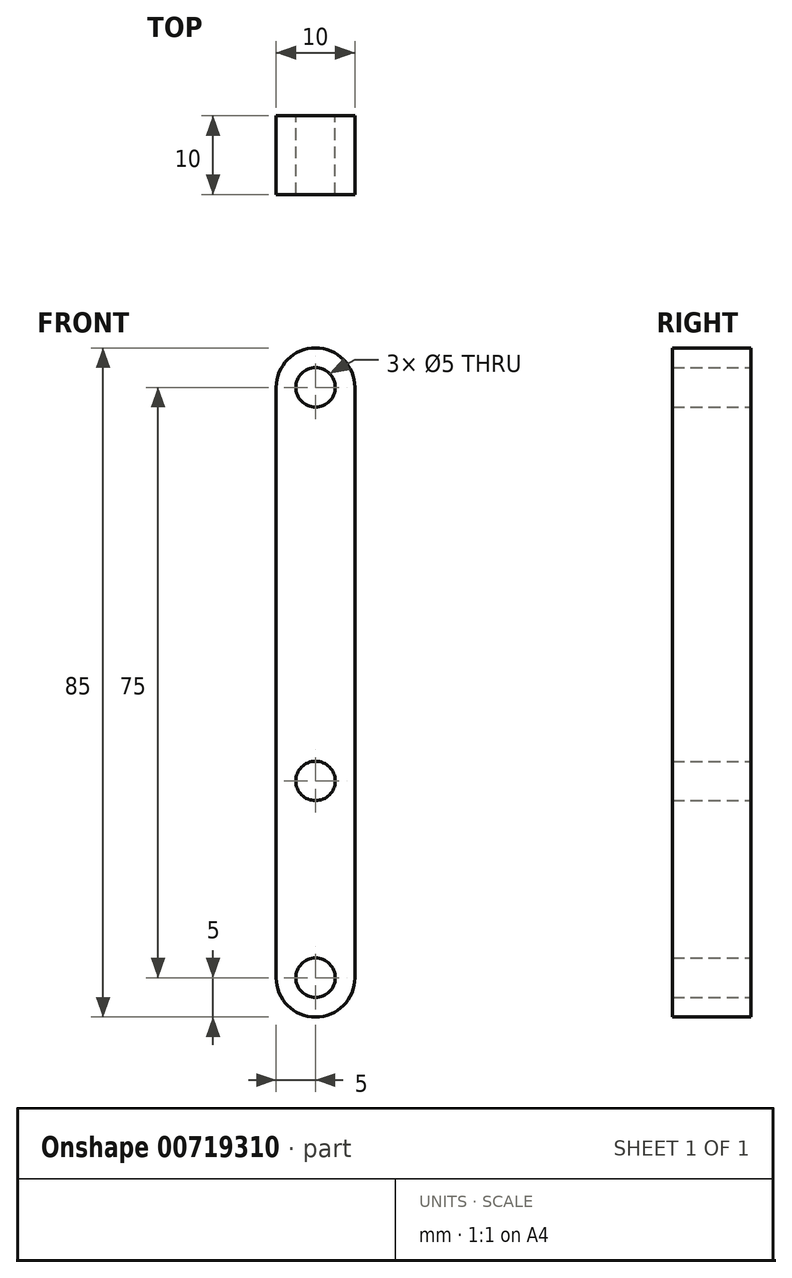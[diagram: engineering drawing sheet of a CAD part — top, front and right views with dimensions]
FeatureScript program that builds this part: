
annotation { "Feature Type Name" : "Feature", "Feature Type Description" : "" }
export const myFeature = defineFeature(function(context is Context, id is Id, definition is map)
    precondition{}
    {
        {
            var Q0;
            Q0=qCreatedBy(makeId("Front.planeOp"),FACE);
            var sketch = newSketch(context, id + "F0", { "sketchPlane" : qUnion([Q0])});
            skArc(sketch, "E0", {"start": v(5, 0) * mm, "mid": v(0, 5) * mm, "end": v(-5, 0) * mm});
            skArc(sketch, "E1", {"start": v(-5, -75) * mm, "mid": v(0, -80) * mm, "end": v(5, -75) * mm});
            skLineSegment(sketch, "E2", {"start": v(5, 0) * mm, "end": v(5, -75) * mm});
            skLineSegment(sketch, "E3", {"start": v(-5, 0) * mm, "end": v(-5, -75) * mm});
            skCircle(sketch, "E4", {"center": v(0, 0) * mm, "radius": 2.5 * mm});
            skCircle(sketch, "E5", {"center": v(0, -75) * mm, "radius": 2.5 * mm});
            skCircle(sketch, "E6", {"center": v(0, -50) * mm, "radius": 2.5 * mm});
            skLineSegment(sketch, "E7", {"start": v(0, 0) * mm, "end": v(0, 0) * mm});
            skLineSegment(sketch, "E8", {"start": v(0, 0) * mm, "end": v(6.63, 0) * mm, "construction": true});
            skSolve(sketch);
        }
        {
            var Q0;
            Q0 = qSketchRegion(id + "F0", true);
            extrude(context, id + "F1", {"entities" : qUnion([Q0]), "depth" : 10 * mm, "offsetDistance" : 25 * mm});
        }
    });
